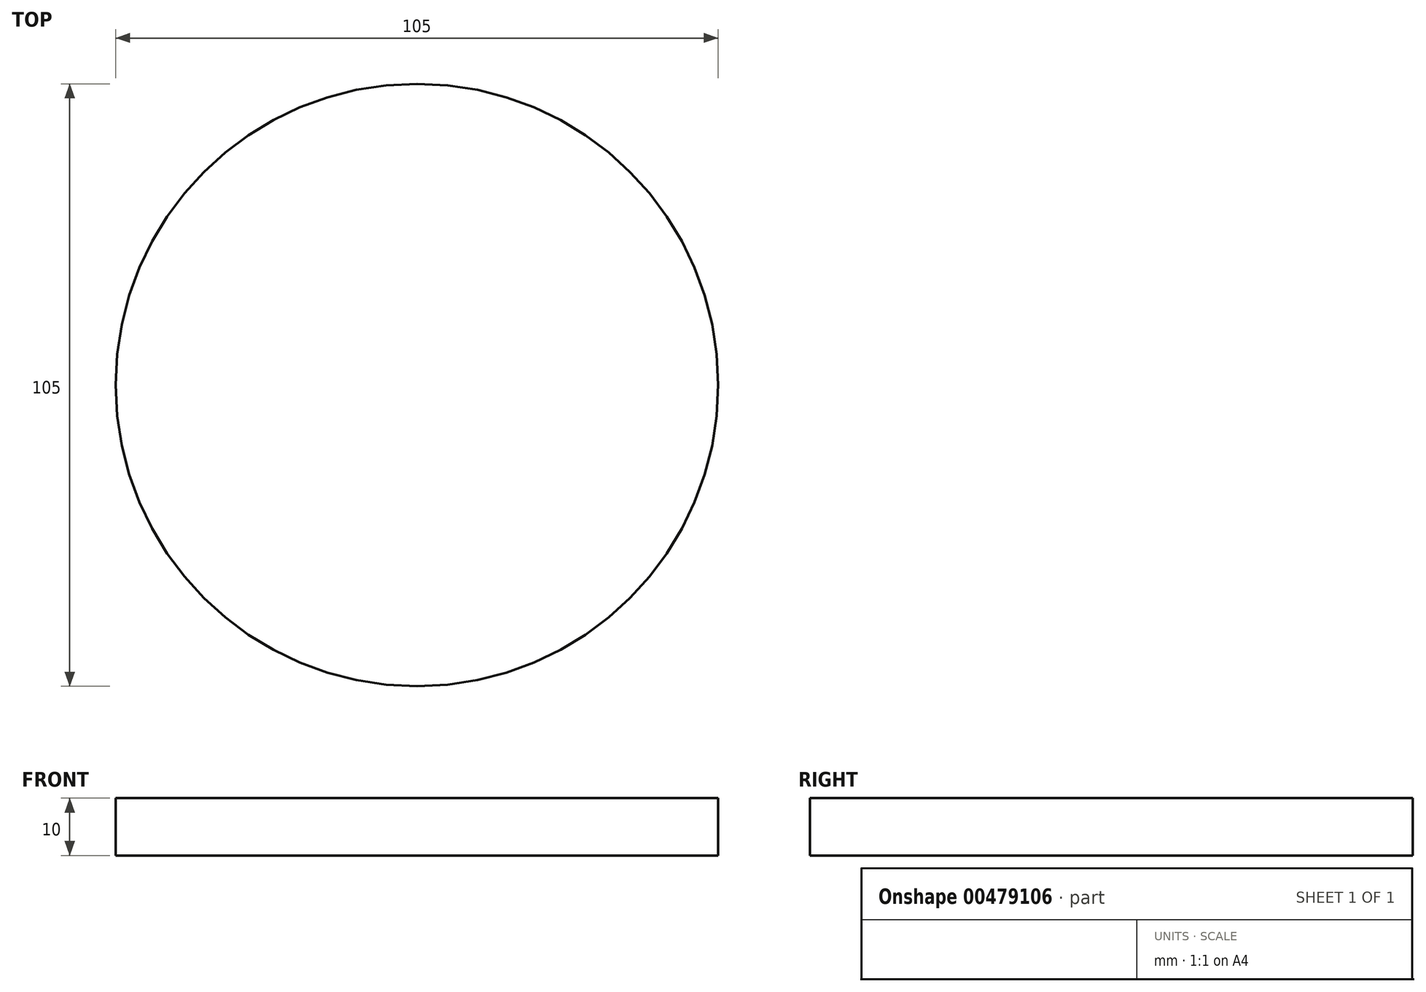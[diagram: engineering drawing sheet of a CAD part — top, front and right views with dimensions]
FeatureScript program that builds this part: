
annotation { "Feature Type Name" : "Feature", "Feature Type Description" : "" }
export const myFeature = defineFeature(function(context is Context, id is Id, definition is map)
    precondition{}
    {
        {
            var Q0;
            Q0=qCreatedBy(makeId("Top.planeOp"),FACE);
            var sketch = newSketch(context, id + "F0", { "sketchPlane" : qUnion([Q0])});
            skCircle(sketch, "E0", {"center": v(0, 0) * mm, "radius": 52.5 * mm});
            skSolve(sketch);
        }
        {
            var Q0;
            Q0=makeQuery(id+"F0.imprint","IMPRINT",FACE,{"disambiguationData":[TD([[makeQuery(id+"F0.imprint","IMPRINT",EDGE,{"derivedFrom":sQuery(id+"F0.wireOp",EDGE,"E0")}),1.0]])]});
            extrude(context, id + "F1", {"entities" : qUnion([Q0]), "depth" : 10 * mm, "offsetDistance" : 25 * mm});
        }
    });
